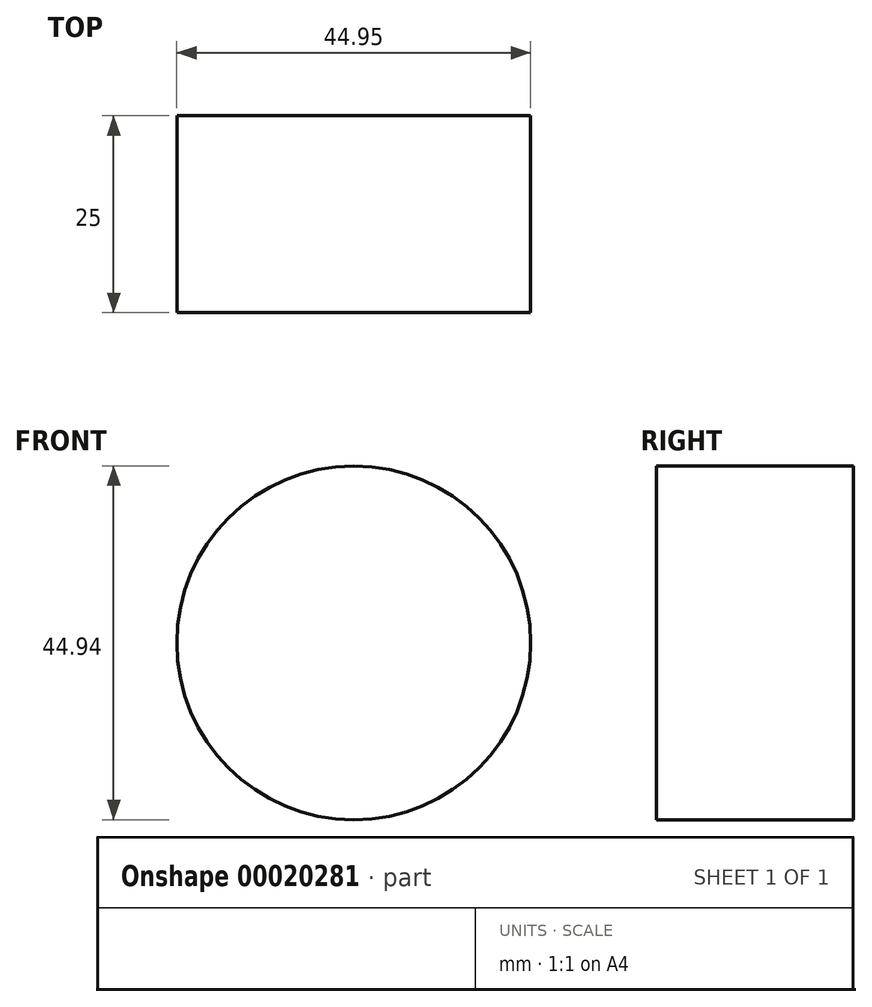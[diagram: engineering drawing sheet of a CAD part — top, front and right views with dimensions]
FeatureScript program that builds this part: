
annotation { "Feature Type Name" : "Feature", "Feature Type Description" : "" }
export const myFeature = defineFeature(function(context is Context, id is Id, definition is map)
    precondition{}
    {
        {
            var Q0;
            Q0=qCreatedBy(makeId("Front.planeOp"),FACE);
            var sketch = newSketch(context, id + "F0", { "sketchPlane" : qUnion([Q0])});
            skCircle(sketch, "E0", {"center": v(30.3, 0) * mm, "radius": 22.47 * mm});
            skSolve(sketch);
        }
        {
            var Q0;
            Q0 = qSketchRegion(id + "F0", true);
            extrude(context, id + "F1", {"entities" : qUnion([Q0]), "depth" : 25 * mm});
        }
    });
